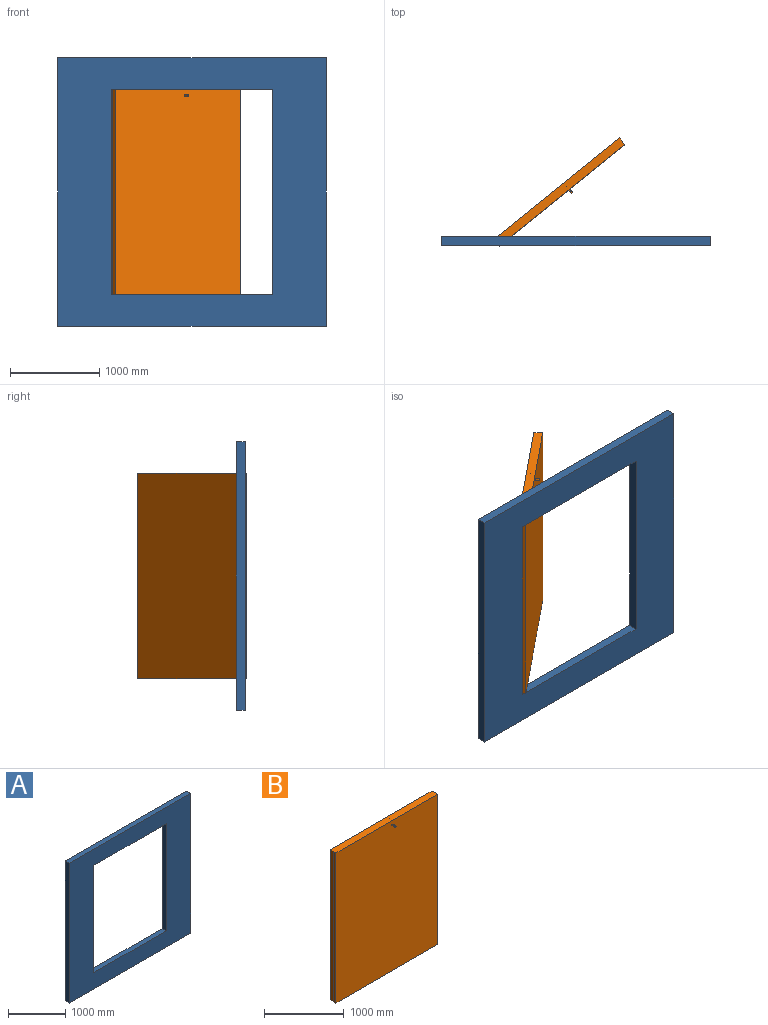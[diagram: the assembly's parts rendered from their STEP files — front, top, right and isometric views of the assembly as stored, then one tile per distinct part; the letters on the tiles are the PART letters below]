
ASSEMBLY  parts=2 mates=1
PART A: 10 faces, bbox 3000x100x3000 mm
  f0: plane 3000x3000mm, normal (0,-1,0), area 4860000mm2, adj f2,f3,f4,f5,f6,f7,f8,f9
  f1: plane 3000x3000mm, normal (0,1,0), area 4860000mm2, adj f2,f3,f4,f5,f6,f7,f8,f9
  f2: plane 3000x100mm, normal (0,0,1), area 300000mm2, adj f0,f1,f3,f5
  f3: plane 3000x100mm, normal (-1,0,0), area 300000mm2, adj f0,f1,f2,f4
  f4: plane 3000x100mm, normal (0,0,-1), area 300000mm2, adj f0,f1,f3,f5
  f5: plane 3000x100mm, normal (1,0,0), area 300000mm2, adj f0,f1,f2,f4
  f6: plane 1800x100mm, normal (0,0,-1), area 180000mm2, adj f0,f1,f7,f9
  f7: plane 2300x100mm, normal (1,0,0), area 230000mm2, adj f0,f1,f6,f8
  f8: plane 1800x100mm, normal (0,0,1), area 180000mm2, adj f0,f1,f7,f9
  f9: plane 2300x100mm, normal (-1,0,0), area 230000mm2, adj f0,f1,f6,f8
PART B: 15 faces, bbox 1800x150x2300 mm
  f0: cylinder r=12.5mm len=50mm, axis (0,1,0), area 1315.4mm2, adj f1,f7,f12,f13
  f1: plane 25x21.71mm, normal (0,-1,0), area 463.4mm2, adj f0,f11,f12,f13
  f2: plane 1800x100mm, normal (0,0,1), area 179992.6mm2, adj f3,f4,f6,f7,f8,f9,f10
  f3: plane 2300x48.75mm, normal (-1,0,0), area 112125mm2, adj f2,f5,f8,f9
  f4: plane 2300x48.75mm, normal (-1,0,0), area 112125mm2, adj f2,f5,f7,f9
  f5: plane 1800x100mm, normal (0,0,-1), area 179992.6mm2, adj f3,f4,f6,f7,f8,f9,f10
  f6: plane 2300x100mm, normal (1,0,0), area 230000mm2, adj f2,f5,f7,f8
  f7: plane 2300x1800mm, normal (0,-1,0), area 4139536.6mm2, adj f0,f2,f4,f5,f6,f11,f12,f13
  f8: plane 2300x1800mm, normal (0,1,0), area 4140000mm2, adj f2,f3,f5,f6
  f9: cylinder r=1.25mm len=2300mm, axis (0,0,1), area 9032.1mm2, adj f2,f3,f4,f5
  f10: cylinder r=1.25mm len=2300mm, axis (0,0,1), area 18064.2mm2, adj f2,f5
  f11: cylinder r=12.5mm len=50mm, axis (0,1,0), area 1315.4mm2, adj f1,f7,f12,f13
  f12: plane 50x12.39mm, normal (0,0,-1), area 506.4mm2, adj f0,f1,f7,f11,f14
  f13: plane 50x12.39mm, normal (0,0,1), area 506.4mm2, adj f0,f1,f7,f11,f14
  f14: cylinder r=6mm len=21.71mm, axis (0,0,1), area 818.6mm2, adj f12,f13
PLACE A t=(-899.96,-418.05,152.32)mm fixed
PLACE B rot(axis=(0,0,1),39deg) t=(-1084.4,128.43,152.32)mm
MATE revolute B.f2 <-> A.f6  axis (0,0,1) through (-1799.96,-418.05,1302.32)mm
